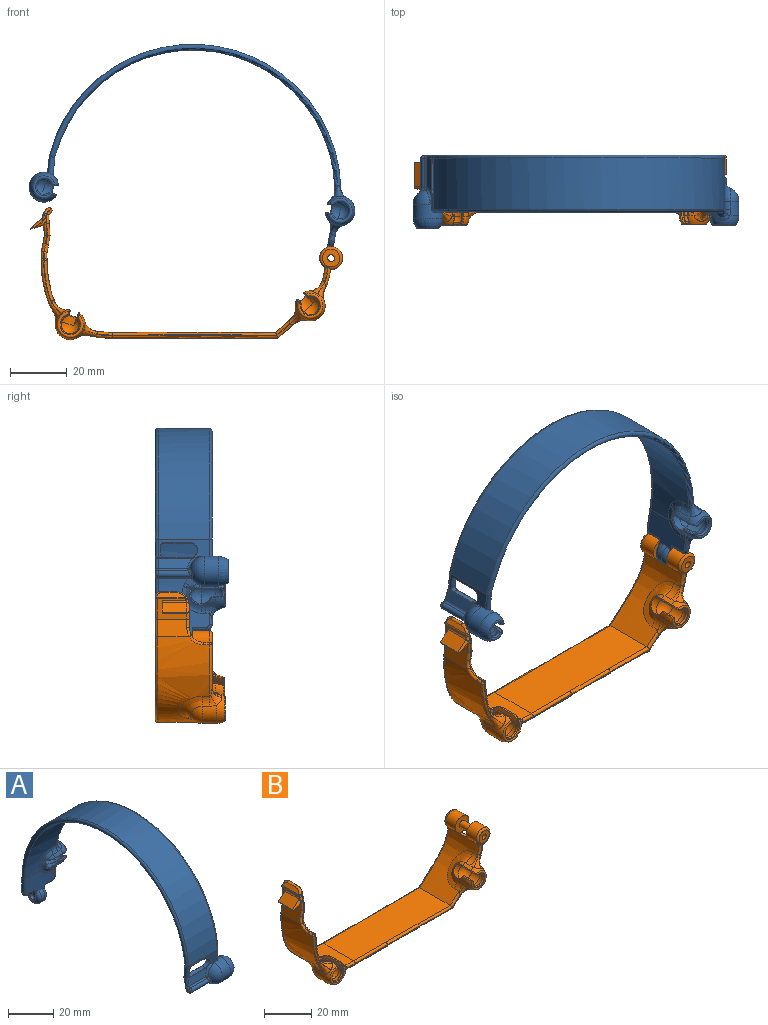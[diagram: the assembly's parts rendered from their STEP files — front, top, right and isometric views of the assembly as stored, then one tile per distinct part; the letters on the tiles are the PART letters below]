
ASSEMBLY  parts=2 mates=1
PART A: 128 faces, bbox 29x116.6x76.7 mm
  f0: cylinder r=5.25mm len=9.98mm, axis (-1,0,0), area 63.7mm2, adj f5,f82,f120,f122,f125,f127
  f1: cylinder r=5.25mm len=3.51mm, axis (-1,0,0), area 6.8mm2, adj f5,f100,f104,f119,f121
  f2: cylinder r=5.25mm len=5mm, axis (-1,0,0), area 9.6mm2, adj f5,f6,f94,f114,f116
  f3: sphere r=3.75mm, area 47.8mm2, adj f4,f7,f87,f103
  f4: cone r=2.84mm half-angle=32.6deg, axis (1,0,0), area 13.6mm2, adj f3,f86,f87,f88,f103,f105
  f5: revolved ~10.5x10.14mm, area 78.1mm2, adj f0,f1,f2,f86,f92,f106,f118,f123
  f6: sphere r=5.25mm, area 3.1mm2, adj f2,f96,f112
  f7: cylinder r=3.75mm len=7.5mm, axis (1,0,0), area 93.5mm2, adj f3,f8,f85,f89,f101
  f8: sphere r=3.75mm, area 55.5mm2, adj f7,f85,f91,f93
  f9: plane 18x11.74mm, normal (0,1,0), area 122.7mm2, adj f11,f14,f15,f37,f38,f60,f62,f63
  f10: plane 20.27x16.01mm, normal (0,-1,0), area 141.9mm2, adj f12,f14,f15,f37,f38,f60,f61,f62
  f11: cylinder r=52.06mm len=104mm, axis (1,0,0), area 2771.6mm2, adj f9,f13,f24,f59,f122,f124
  f12: cylinder r=50.06mm len=100mm, axis (1,0,0), area 2684.3mm2, adj f10,f13,f28,f59,f108,f110,f112,f113
  f13: torus R=51.06mm, axis (-1,0,0), area 457.9mm2, adj f11,f12,f64,f65,f116,f118,f120
  f14: cylinder r=1mm len=3.94mm, axis (0,0,-1), area 8.3mm2, adj f9,f10,f67,f68,f121,f123,f125
  f15: cylinder r=4mm len=8mm, axis (1,0,0), area 46.1mm2, adj f9,f10,f79,f80
  f16: cylinder r=5.25mm len=10.5mm, axis (1,0,0), area 135.3mm2, adj f17,f24,f30,f43,f46,f47,f64,f70
  f17: revolved ~10.49x10.21mm, area 97.9mm2, adj f16,f39,f42,f48
  f18: cone r=3.42mm half-angle=35.3deg, axis (1,0,0), area 11mm2, adj f19,f39,f40,f50
  f19: sphere r=3.75mm, area 55.1mm2, adj f18,f20,f31,f33,f40,f50
  f20: cylinder r=3.75mm len=7.5mm, axis (-1,0,0), area 94.9mm2, adj f19,f21,f31,f32,f33
  f21: sphere r=3.75mm, area 57.4mm2, adj f20,f32,f33
  f22: cylinder r=1.3mm len=11.27mm, axis (1,0,0), area 37.9mm2, adj f23,f53,f54,f71
  f23: cylinder r=1.8mm len=11.38mm, axis (1,0,0), area 28.9mm2, adj f22,f27,f52,f71
  f24: plane 18.05x6.4mm, normal (0,-1,-0.08), area 47.3mm2, adj f11,f16,f34,f35,f51,f58,f64,f74
  f25: plane 18x6.32mm, normal (0,1,0.08), area 46.8mm2, adj f28,f34,f35,f36,f51,f58,f64,f70
  f26: plane 12.36x3.83mm, normal (0,-0.98,0.21), area 43.1mm2, adj f54,f55,f74,f75
  f27: plane 14.84x6.26mm, normal (0,0.98,-0.21), area 75.5mm2, adj f23,f30,f55,f70,f71
  f28: plane 18x0.04mm, normal (0,0.84,0.55), area 0.8mm2, adj f12,f25,f57,f65
  f29: plane 2.2x1.72mm, normal (-1,0,0), area 1.2mm2, adj f52,f53,f55,f56
  f30: sphere r=5.25mm, area 110.6mm2, adj f16,f27,f44,f45,f70,f71,f75
  f31: plane 4.91x2.41mm, normal (0,0.04,1), area 5.9mm2, adj f19,f20,f32,f47,f48,f49,f50
  f32: cylinder r=3.75mm len=7.19mm, axis (0,-1,0.04), area 28.6mm2, adj f20,f21,f31,f33,f45,f46,f47
  f33: plane 11.85x4.62mm, normal (0,-0.04,-1), area 14.9mm2, adj f19,f20,f21,f32,f40,f41,f42,f43
  f34: plane 3.64x2.26mm, normal (1,0,0), area 7mm2, adj f24,f25,f76,f77
  f35: plane 9.04x1.99mm, normal (0,0.08,-1), area 18.1mm2, adj f24,f25,f77,f78
  f36: plane 9.01x2mm, normal (0,-0.08,1), area 18.1mm2, adj f25,f51,f74,f76
  f37: plane 6.9x4mm, normal (-1,0,0), area 12.7mm2, adj f9,f10,f62,f80,f81
  f38: plane 6.9x4mm, normal (1,0,0), area 12.7mm2, adj f9,f10,f66,f79,f81
  f39: torus R=3.5mm, axis (-1,0,0), area 19.5mm2, adj f17,f18,f41,f49
  f40: bspline ~2.06x1.78mm, area 0.3mm2, adj f18,f19,f33,f41
  f41: bspline ~1.15x0.5mm, area 0.4mm2, adj f33,f39,f40,f42
  f42: bspline ~5.4x2.59mm, area 2.2mm2, adj f17,f33,f41,f43
  f43: cylinder r=0.3mm len=5mm, axis (1,0,0), area 2.9mm2, adj f16,f33,f42,f44
  f44: torus R=4.61mm, axis (0,-0.04,-1), area 2.5mm2, adj f30,f33,f43,f45
  f45: torus R=4.05mm, axis (0,-1,0.04), area 6mm2, adj f30,f32,f33,f44,f46
  f46: bspline ~4.49x2.95mm, area 3.1mm2, adj f16,f32,f45,f47
  f47: cylinder r=0.3mm len=1.57mm, axis (1,0,0), area 0.9mm2, adj f16,f31,f32,f46,f48
  f48: bspline ~5.4x2.59mm, area 2.2mm2, adj f17,f31,f47,f49
  f49: bspline ~1.21x0.48mm, area 0.4mm2, adj f31,f39,f48,f50
  f50: bspline ~2.06x1.79mm, area 0.3mm2, adj f18,f19,f31,f49
  f51: cylinder r=2.99mm len=3.14mm, axis (0,1,0.08), area 9.4mm2, adj f24,f25,f36,f74,f78
  f52: torus R=0.8mm, axis (-1,0,0), area 3.2mm2, adj f23,f29,f53,f55
  f53: torus R=0.3mm, axis (-1,0,0), area 4.1mm2, adj f22,f29,f52,f56
  f54: cylinder r=1mm len=10.28mm, axis (1,0,0), area 11.5mm2, adj f22,f26,f56,f73
  f55: cylinder r=1mm len=6.62mm, axis (0,-0.21,-0.98), area 16.2mm2, adj f26,f27,f29,f52,f56,f69,f72
  f56: torus R=2mm, axis (-1,0,0), area 2.4mm2, adj f29,f53,f54,f55
  f57: cylinder r=1mm len=1.04mm, axis (0,0.55,-0.84), area 0.1mm2, adj f28,f58,f59
  f58: cylinder r=1mm len=6.8mm, axis (0,0.08,-1), area 19.9mm2, adj f24,f25,f57,f59,f69,f72
  f59: torus R=51.06mm, axis (-1,0,0), area 493.5mm2, adj f11,f12,f57,f58,f60
  f60: cylinder r=1mm len=7.83mm, axis (0,0,1), area 24.6mm2, adj f9,f10,f59,f61,f63
  f61: bspline ~2.69x2.5mm, area 4.4mm2, adj f10,f60,f62,f63
  f62: cylinder r=1mm len=5mm, axis (-1,0,0), area 15.7mm2, adj f9,f10,f37,f61,f63
  f63: bspline ~2.45x2.45mm, area 3.7mm2, adj f9,f60,f61,f62
  f64: cylinder r=1mm len=6.86mm, axis (0,-0.08,1), area 19.2mm2, adj f13,f16,f24,f25,f65,f70
  f65: cylinder r=1mm len=1.04mm, axis (0,-0.55,0.84), area 0.1mm2, adj f13,f28,f64
  f66: cylinder r=1mm len=5mm, axis (1,0,0), area 15.7mm2, adj f9,f10,f38,f67,f68
  f67: bspline ~2.69x2.5mm, area 4.4mm2, adj f10,f14,f66,f68
  f68: bspline ~2.45x2.45mm, area 3.7mm2, adj f9,f14,f66,f67
  f69: sphere r=1mm, area 0.3mm2, adj f55,f58,f70
  f70: cylinder r=1mm len=18mm, axis (1,0,0), area 4.6mm2, adj f16,f25,f27,f30,f64,f69
  f71: bspline ~3.86x3.82mm, area 5.4mm2, adj f22,f23,f27,f30,f73
  f72: bspline ~1.04x1.03mm, area 0.2mm2, adj f55,f58,f74
  f73: sphere r=1mm, area 0.9mm2, adj f54,f71,f75
  f74: cylinder r=1mm len=13.23mm, axis (-1,0,0), area 2.4mm2, adj f24,f26,f36,f51,f72,f75,f76
  f75: torus R=6.01mm, axis (0,0.98,-0.21), area 7.9mm2, adj f16,f24,f26,f30,f73,f74
  f76: cylinder r=1mm len=2.08mm, axis (0,-1,-0.08), area 3.1mm2, adj f24,f25,f34,f36,f74
  f77: cylinder r=1mm len=2.07mm, axis (0,1,0.08), area 3.1mm2, adj f24,f25,f34,f35
  f78: cylinder r=3mm len=2.96mm, axis (0,-1,-0.08), area 8.4mm2, adj f24,f25,f35,f51
  f79: torus R=2mm, axis (1,0,0), area 54.4mm2, adj f9,f10,f15,f38
  f80: torus R=2mm, axis (-1,0,0), area 54.4mm2, adj f9,f10,f15,f37
  f81: cylinder r=1.25mm len=6mm, axis (1,0,0), area 47.1mm2, adj f37,f38
  f82: sphere r=5.25mm, area 50.1mm2, adj f0,f124,f126
  f83: plane 11.39x2.97mm, normal (0,0,-1), area 11.8mm2, adj f87,f88,f89,f90,f91,f92,f94,f95
  f84: plane 4.52x1.96mm, normal (0,0,1), area 4.6mm2, adj f99,f101,f103,f104,f105,f106,f107
  f85: cylinder r=3.75mm len=7.11mm, axis (0,1,0), area 29.1mm2, adj f7,f8,f95,f98,f99,f100
  f86: torus R=3.81mm, axis (1,0,0), area 24.2mm2, adj f4,f5,f90,f107
  f87: torus R=3.63mm, axis (0,0,-1), area 0.9mm2, adj f3,f4,f83,f88,f89
  f88: bspline ~2.48x1.92mm, area 0.3mm2, adj f4,f83,f87,f90
  f89: cylinder r=0.3mm len=5mm, axis (1,0,0), area 1.7mm2, adj f7,f83,f87,f91
  f90: bspline ~1.26x0.51mm, area 0.5mm2, adj f83,f86,f88,f92
  f91: torus R=3.63mm, axis (0,0,-1), area 1.3mm2, adj f8,f83,f89,f93
  f92: bspline ~5.45x2.16mm, area 2mm2, adj f5,f83,f90,f94
  f93: bspline ~1.64x0.52mm, area 0.2mm2, adj f8,f91,f95
  f94: cylinder r=0.3mm len=5mm, axis (-1,0,0), area 2.9mm2, adj f2,f83,f92,f96
  f95: cylinder r=0.3mm len=3.29mm, axis (0,1,0), area 0.8mm2, adj f83,f85,f93,f97
  f96: torus R=4.61mm, axis (0,0,-1), area 2.2mm2, adj f6,f83,f94,f97,f110
  f97: bspline ~0.95x0.83mm, area 0.3mm2, adj f95,f96,f98,f108,f109
  f98: torus R=4.05mm, axis (0,1,0), area 5.3mm2, adj f85,f97,f100,f109,f113,f115
  f99: cylinder r=0.3mm len=1.25mm, axis (0,1,0), area 0.4mm2, adj f84,f85,f101,f102
  f100: bspline ~4.49x3.03mm, area 3mm2, adj f1,f85,f98,f102,f117
  f101: cylinder r=0.3mm len=1.64mm, axis (1,0,0), area 0.5mm2, adj f7,f84,f99,f103
  f102: sphere r=0.3mm, area 0.1mm2, adj f99,f100,f104
  f103: torus R=3.63mm, axis (0,0,1), area 0.9mm2, adj f3,f4,f84,f101,f105
  f104: cylinder r=0.3mm len=1.37mm, axis (-1,0,0), area 0.8mm2, adj f1,f84,f102,f106
  f105: bspline ~2.48x1.92mm, area 0.3mm2, adj f4,f84,f103,f107
  f106: bspline ~5.45x2.16mm, area 2mm2, adj f5,f84,f104,f107
  f107: bspline ~1.23x0.51mm, area 0.5mm2, adj f84,f86,f105,f106
  f108: bspline ~2.88x1.23mm, area 0.5mm2, adj f12,f97,f109,f110,f111
  f109: bspline ~0.46x0.45mm, area 0.1mm2, adj f97,f98,f108,f111
  f110: bspline ~3.27x2.63mm, area 2.3mm2, adj f12,f96,f108,f112
  f111: bspline ~2.55x1.03mm, area 0.8mm2, adj f108,f109,f113
  f112: bspline ~7.68x5.32mm, area 18.6mm2, adj f6,f12,f110,f114
  f113: bspline ~7.49x3.41mm, area 13.3mm2, adj f12,f98,f111,f115
  f114: cylinder r=4mm len=3.45mm, axis (1,0,0), area 10.2mm2, adj f2,f12,f112,f116
  f115: torus R=6.97mm, axis (0,-1,0), area 18.3mm2, adj f10,f98,f113,f117
  f116: bspline ~4.09x3.8mm, area 5.1mm2, adj f2,f13,f114,f118
  f117: bspline ~3.12x2.19mm, area 4.7mm2, adj f10,f100,f115,f119
  f118: bspline ~5.33x5.11mm, area 16.9mm2, adj f5,f13,f116,f120
  f119: cylinder r=4mm len=3.04mm, axis (-1,0,0), area 4.4mm2, adj f1,f10,f117,f121
  f120: bspline ~3.9x3.35mm, area 5.6mm2, adj f0,f13,f118,f122
  f121: bspline ~3.65x3.63mm, area 4.9mm2, adj f1,f14,f119,f123
  f122: cylinder r=4mm len=2.97mm, axis (-1,0,0), area 11.6mm2, adj f0,f11,f120,f124
  f123: bspline ~5.37x4.9mm, area 17.1mm2, adj f5,f14,f121,f125
  f124: bspline ~12.73x10.22mm, area 54.8mm2, adj f11,f82,f122,f126
  f125: bspline ~3.99x3.95mm, area 5.8mm2, adj f0,f14,f123,f127
  f126: torus R=8.34mm, axis (0,-1,0), area 33.6mm2, adj f9,f82,f124,f127
  f127: cylinder r=4mm len=3.61mm, axis (-1,0,0), area 12.4mm2, adj f0,f9,f125,f126
PART B: 192 faces, bbox 111.3x26.9x47.9 mm
  f0: bspline ~3.23x3.2mm, area 0.8mm2, adj f22,f187,f191
  f1: cylinder r=5.25mm len=5mm, axis (0,-1,0), area 16.9mm2, adj f14,f18,f136,f186,f188
  f2: cylinder r=5.25mm len=1.5mm, axis (0,-1,0), area 0.6mm2, adj f18,f128,f131,f191
  f3: cylinder r=5.25mm len=5mm, axis (0,-1,0), area 8.8mm2, adj f104,f105,f109,f148,f170,f172
  f4: cylinder r=5.25mm len=5mm, axis (0,-1,0), area 9.5mm2, adj f104,f105,f143,f171,f173
  f5: cylinder r=4mm len=8mm, axis (0,-1,0), area 134.9mm2, adj f7,f8,f48,f155
  f6: plane 68.31x4.23mm, normal (0,-1,0), area 14mm2, adj f9,f11,f24,f26,f83,f88,f166,f184
  f7: extruded ~24.21x18.51mm, area 414.3mm2, adj f5,f11,f12,f34,f35,f50,f154,f159
  f8: extruded ~22.82x18.2mm, area 376.3mm2, adj f5,f9,f10,f35,f36,f49,f154,f155
  f9: bspline ~8.48x7.61mm, area 9.3mm2, adj f6,f8,f83,f168,f170
  f10: bspline ~9.06x2.75mm, area 7.3mm2, adj f8,f13,f82,f169,f171
  f11: bspline ~7.89x7.09mm, area 9.9mm2, adj f6,f7,f88,f162,f164
  f12: bspline ~9.59x3.31mm, area 9.6mm2, adj f7,f13,f82,f163,f165
  f13: plane 11.85x6.2mm, normal (0,-1,0), area 26.5mm2, adj f10,f12,f82,f157,f167
  f14: sphere r=5.25mm, area 10.5mm2, adj f1,f132,f134,f135,f190
  f15: cylinder r=5.25mm len=8.29mm, axis (0,-1,0), area 60.9mm2, adj f18,f95,f175,f176,f179,f181
  f16: sphere r=3.75mm, area 37.8mm2, adj f19,f99,f117,f122
  f17: cone r=3mm half-angle=42.1deg, axis (0,-1,0), area 7.5mm2, adj f115,f116,f117,f118
  f18: revolved ~10.49x10.49mm, area 63mm2, adj f1,f2,f15,f116,f126,f137,f178,f180
  f19: cylinder r=3.75mm len=7.5mm, axis (0,1,0), area 93.9mm2, adj f16,f96,f99,f124,f125
  f20: plane 15.17x3.07mm, normal (0,-1,0), area 3.1mm2, adj f23,f25,f91,f180
  f21: extruded ~30.08x25.01mm, area 673.2mm2, adj f25,f26,f33,f34,f54,f92,f94,f175
  f22: extruded ~27.88x23mm, area 583.4mm2, adj f0,f23,f24,f36,f37,f53,f79,f84
  f23: bspline ~16.59x3.95mm, area 20.3mm2, adj f20,f22,f89,f182,f191
  f24: bspline ~7.08x1.52mm, area 7.7mm2, adj f6,f22,f83,f185,f186
  f25: bspline ~20.35x6.19mm, area 24.6mm2, adj f20,f21,f93,f176,f178
  f26: bspline ~10.95x2.43mm, area 10.2mm2, adj f6,f21,f88,f181,f183
  f27: plane 7.42x0.74mm, normal (0,-1,0), area 1.5mm2, adj f45,f46,f74,f76,f85,f87
  f28: plane 8.6x4.05mm, normal (-0.65,0,0.76), area 45.7mm2, adj f29,f42,f71,f75,f78
  f29: plane 9.13x0.33mm, normal (-0.96,0,-0.29), area 2.8mm2, adj f28,f30,f42,f78,f81
  f30: plane 8.6x4.5mm, normal (0.29,0,-0.96), area 40.4mm2, adj f29,f32,f42,f81
  f31: plane 104.17x43.26mm, normal (0,1,0), area 54.8mm2, adj f47,f48,f49,f50,f51,f52,f53,f54
  f32: plane 10.2x7.12mm, normal (-1,0,-0.07), area 45.4mm2, adj f30,f33,f42,f60,f66,f70,f71,f85
  f33: plane 11.13x6.21mm, normal (-0.99,0,0.17), area 65.2mm2, adj f21,f32,f56,f87,f90,f92
  f34: cylinder r=4958.52mm len=58.24mm, axis (0,-1,0), area 1060mm2, adj f7,f21,f52,f88
  f35: cylinder r=4mm len=8mm, axis (0,-1,0), area 134.9mm2, adj f7,f8,f82,f156
  f36: cylinder r=4960.52mm len=57.49mm, axis (0,-1,0), area 1046.2mm2, adj f8,f22,f51,f83
  f37: plane 11.09x6.31mm, normal (0.99,0,-0.17), area 66.3mm2, adj f22,f38,f55,f76,f79
  f38: plane 10.25x7.07mm, normal (1,0,0.07), area 70.4mm2, adj f37,f39,f57,f69,f72,f74
  f39: plane 9.32x1.21mm, normal (0.77,0,-0.63), area 12.8mm2, adj f38,f61,f64,f67,f69
  f40: plane 5x0.15mm, normal (0.63,0,0.77), area 1mm2, adj f45,f47,f62,f67
  f41: plane 9.62x1.55mm, normal (-0.77,0,0.63), area 17mm2, adj f58,f59,f62,f65,f66
  f42: plane 4.59x4.5mm, normal (0,1,0), area 7.1mm2, adj f28,f29,f30,f32,f71
  f43: plane 2.1x0.2mm, normal (-0.07,0,1), area 0.4mm2, adj f46,f86,f91,f94
  f44: plane 1.87x1.07mm, normal (0,-1,0), area 0.6mm2, adj f45,f78,f81
  f45: cylinder r=5mm len=5.3mm, axis (-0.77,0,0.63), area 2.7mm2, adj f27,f40,f44,f65,f69,f70,f72,f73
  f46: cylinder r=5mm len=5.08mm, axis (1,0,0.07), area 1.6mm2, adj f27,f43,f79,f84,f90,f92
  f47: cylinder r=2mm len=2mm, axis (0.77,0,-0.63), area 0.6mm2, adj f31,f40,f58,f64
  f48: torus R=3.1mm, axis (0,1,0), area 31.1mm2, adj f5,f31,f49,f50
  f49: bspline ~26.51x19.23mm, area 42.7mm2, adj f8,f31,f48,f51
  f50: bspline ~26.74x19.92mm, area 44.3mm2, adj f7,f31,f48,f52
  f51: torus R=4959.62mm, axis (0,1,0), area 81.5mm2, adj f31,f36,f49,f53
  f52: torus R=4959.42mm, axis (0,1,0), area 82.1mm2, adj f31,f34,f50,f54
  f53: bspline ~29.18x24.25mm, area 60.1mm2, adj f22,f31,f51,f55
  f54: bspline ~30.56x25.39mm, area 63.2mm2, adj f21,f31,f52,f56
  f55: cylinder r=0.9mm len=6.53mm, axis (-0.17,0,-0.99), area 9mm2, adj f31,f37,f53,f57
  f56: cylinder r=0.9mm len=6.46mm, axis (0.17,0,0.99), area 8.9mm2, adj f31,f33,f54,f60
  f57: cylinder r=0.9mm len=7.35mm, axis (0.07,0,-1), area 10mm2, adj f31,f38,f55,f61
  f58: torus R=1.1mm, axis (-0.77,0,0.63), area 3.7mm2, adj f41,f47,f59,f62
  f59: cylinder r=0.9mm len=1.27mm, axis (0.63,0,0.77), area 1.3mm2, adj f31,f41,f58,f63
  f60: cylinder r=0.9mm len=7.29mm, axis (-0.07,0,1), area 10.2mm2, adj f31,f32,f56,f63
  f61: cylinder r=0.9mm len=1.22mm, axis (-0.63,0,-0.77), area 0.9mm2, adj f31,f39,f57,f64
  f62: cylinder r=0.9mm len=5mm, axis (0,-1,0), area 7.1mm2, adj f40,f41,f58,f65
  f63: sphere r=0.9mm, area 0.5mm2, adj f59,f60,f66
  f64: torus R=1.1mm, axis (-0.77,0,0.63), area 3.7mm2, adj f39,f47,f61,f67
  f65: torus R=4.1mm, axis (-0.77,0,0.63), area 6.8mm2, adj f41,f45,f62,f68
  f66: cylinder r=0.9mm len=9.62mm, axis (0,-1,0), area 6.6mm2, adj f32,f41,f63,f68
  f67: cylinder r=0.9mm len=5mm, axis (0,1,0), area 7.1mm2, adj f39,f40,f64,f69
  f68: sphere r=0.9mm, area 0.6mm2, adj f65,f66,f70
  f69: torus R=4.1mm, axis (-0.77,0,0.63), area 6.4mm2, adj f38,f39,f45,f67,f72
  f70: bspline ~2.44x1.83mm, area 1mm2, adj f32,f45,f68,f73
  f71: cylinder r=0.9mm len=8.6mm, axis (0,1,0), area 7.1mm2, adj f28,f32,f42,f73
  f72: bspline ~3.36x1.53mm, area 4mm2, adj f38,f45,f69,f74
  f73: bspline ~2.18x1.64mm, area 2.1mm2, adj f45,f70,f71,f75
  f74: cylinder r=0.9mm len=4.36mm, axis (-0.07,0,1), area 6mm2, adj f27,f38,f72,f76
  f75: bspline ~1.4x1.4mm, area 0.3mm2, adj f28,f45,f73,f78
  f76: cylinder r=0.9mm len=3.31mm, axis (0.17,0,0.99), area 4.5mm2, adj f27,f37,f74,f79
  f77: bspline ~2.14x1.51mm, area 0mm2, adj f45,f80,f81
  f78: cylinder r=0.9mm len=4.54mm, axis (-0.76,0,-0.65), area 5.8mm2, adj f28,f29,f44,f75,f81
  f79: bspline ~3.37x1.68mm, area 4.5mm2, adj f22,f37,f46,f76,f84
  f80: bspline ~2.25x1.01mm, area 0.1mm2, adj f45,f77,f81,f85
  f81: cylinder r=0.9mm len=5.54mm, axis (0.96,0,0.29), area 5.7mm2, adj f29,f30,f44,f77,f78,f80,f85
  f82: torus R=3.1mm, axis (0,1,0), area 31.1mm2, adj f10,f12,f13,f35
  f83: torus R=4959.62mm, axis (0,1,0), area 81.5mm2, adj f6,f9,f24,f36
  f84: bspline ~5.5x3.47mm, area 7.8mm2, adj f22,f46,f79,f86
  f85: cylinder r=0.9mm len=4.41mm, axis (0.07,0,-1), area 5.5mm2, adj f27,f32,f80,f81,f87
  f86: cylinder r=0.9mm len=2.1mm, axis (0,-1,0), area 3.1mm2, adj f22,f43,f84,f89
  f87: cylinder r=0.9mm len=3.23mm, axis (-0.17,0,-0.99), area 4.3mm2, adj f27,f33,f85,f90
  f88: torus R=4959.42mm, axis (0,1,0), area 82.1mm2, adj f6,f11,f26,f34
  f89: sphere r=0.9mm, area 1.3mm2, adj f23,f86,f91
  f90: bspline ~4.9x2.07mm, area 4.2mm2, adj f33,f46,f87,f92
  f91: cylinder r=0.9mm len=0.91mm, axis (-1,0,-0.07), area 0.3mm2, adj f20,f43,f89,f93
  f92: bspline ~6.88x4.28mm, area 7.4mm2, adj f21,f33,f46,f90,f94
  f93: sphere r=0.9mm, area 0.8mm2, adj f25,f91,f94
  f94: cylinder r=0.9mm len=2.1mm, axis (0,-1,0), area 2.9mm2, adj f21,f43,f92,f93
  f95: sphere r=5.25mm, area 346.4mm2, adj f15,f177
  f96: sphere r=3.75mm, area 56mm2, adj f19,f98,f99,f133
  f97: plane 4.16x1.55mm, normal (0.95,0,-0.31), area 4mm2, adj f118,f120,f122,f123,f124,f126,f128,f129
  f98: cylinder r=3.75mm len=7.11mm, axis (-0.31,0,-0.95), area 28.5mm2, adj f96,f125,f129,f131,f132,f133
  f99: plane 12.16x4.42mm, normal (-0.95,0,0.31), area 13.4mm2, adj f16,f19,f96,f115,f117,f133,f135,f136
  f100: sphere r=5.25mm, area 0mm2, adj f101,f159
  f101: cylinder r=5.25mm len=7.36mm, axis (0,-1,0), area 57mm2, adj f100,f104,f160,f161,f162,f163
  f102: sphere r=3.75mm, area 40.5mm2, adj f106,f110,f112,f151
  f103: cone r=2.84mm half-angle=49.9deg, axis (0,-1,0), area 5.2mm2, adj f111,f112,f113,f114
  f104: torus R=0mm, axis (0,-1,0), area 65.9mm2, adj f3,f4,f101,f113,f142,f147,f164,f165
  f105: sphere r=5.25mm, area 8.9mm2, adj f3,f4,f109,f144,f174
  f106: cylinder r=3.75mm len=7.5mm, axis (0,1,0), area 94.5mm2, adj f102,f107,f109,f110,f150
  f107: sphere r=3.75mm, area 57.4mm2, adj f106,f109,f110
  f108: plane 4.18x1.24mm, normal (0.71,0,0.71), area 4mm2, adj f114,f146,f147,f148,f149,f150,f151,f152
  f109: cylinder r=3.75mm len=7.46mm, axis (0.71,0,-0.71), area 37.1mm2, adj f3,f105,f106,f107,f110,f144,f148,f149
  f110: plane 11.41x3.43mm, normal (-0.71,0,-0.71), area 14mm2, adj f102,f106,f107,f109,f111,f112,f141,f142
  f111: bspline ~2x1.97mm, area 0.5mm2, adj f103,f110,f112,f140
  f112: torus R=3.66mm, axis (0,1,0), area 13.9mm2, adj f102,f103,f110,f111,f152,f153
  f113: torus R=3.89mm, axis (0,1,0), area 21.3mm2, adj f103,f104,f140,f141,f145,f146
  f114: bspline ~1.63x1.63mm, area 0.5mm2, adj f103,f108,f145,f153
  f115: bspline ~2.69x2.65mm, area 0.6mm2, adj f17,f99,f117,f139
  f116: torus R=4.04mm, axis (0,1,0), area 25.4mm2, adj f17,f18,f121,f123,f138,f139
  f117: torus R=3.76mm, axis (0,1,0), area 12.6mm2, adj f16,f17,f99,f115,f119,f120
  f118: bspline ~2.29x2.12mm, area 0.5mm2, adj f17,f97,f119,f121
  f119: bspline ~0.74x0.42mm, area 0.1mm2, adj f117,f118,f120
  f120: bspline ~0.3x0.25mm, area 0mm2, adj f97,f117,f119,f122
  f121: bspline ~0.8x0.65mm, area 0.2mm2, adj f116,f118,f123
  f122: torus R=3.63mm, axis (0.95,0,-0.31), area 0.7mm2, adj f16,f97,f120,f124
  f123: bspline ~0.63x0.49mm, area 0.2mm2, adj f97,f116,f121,f126
  f124: cylinder r=0.3mm len=1.37mm, axis (0,1,0), area 0.5mm2, adj f19,f97,f122,f127
  f125: bspline ~3.79x3.48mm, area 0.7mm2, adj f19,f98,f127
  f126: bspline ~5.04x1.62mm, area 1.7mm2, adj f18,f97,f123,f128
  f127: sphere r=0.3mm, area 0mm2, adj f124,f125,f129
  f128: cylinder r=0.3mm len=1.37mm, axis (0,-1,0), area 0.8mm2, adj f2,f97,f126,f130
  f129: cylinder r=0.3mm len=0.99mm, axis (-0.31,0,-0.95), area 0.3mm2, adj f97,f98,f127,f130
  f130: sphere r=0.3mm, area 0.1mm2, adj f128,f129,f131
  f131: bspline ~4.49x3.44mm, area 1.8mm2, adj f2,f98,f130,f132,f187,f191
  f132: torus R=4.05mm, axis (-0.31,0,-0.95), area 4.2mm2, adj f14,f98,f131,f134,f189
  f133: cylinder r=0.3mm len=3.19mm, axis (-0.31,0,-0.95), area 0.9mm2, adj f96,f98,f99,f134
  f134: bspline ~0.92x0.83mm, area 0.4mm2, adj f14,f132,f133,f135
  f135: torus R=4.61mm, axis (0.95,0,-0.31), area 2.2mm2, adj f14,f99,f134,f136
  f136: cylinder r=0.3mm len=5mm, axis (0,-1,0), area 2.9mm2, adj f1,f99,f135,f137
  f137: bspline ~5.04x1.62mm, area 1.7mm2, adj f18,f99,f136,f138
  f138: bspline ~0.69x0.55mm, area 0.2mm2, adj f99,f116,f137,f139
  f139: bspline ~1x0.43mm, area 0.2mm2, adj f115,f116,f138
  f140: bspline ~0.99x0.62mm, area 0.2mm2, adj f111,f113,f141
  f141: bspline ~0.59x0.58mm, area 0.1mm2, adj f110,f113,f140,f142
  f142: bspline ~4.84x1.53mm, area 1.8mm2, adj f104,f110,f141,f143
  f143: cylinder r=0.3mm len=5mm, axis (0,-1,0), area 2.9mm2, adj f4,f110,f142,f144
  f144: torus R=4.61mm, axis (0.71,0,0.71), area 2.2mm2, adj f105,f109,f110,f143
  f145: bspline ~0.99x0.62mm, area 0.2mm2, adj f113,f114,f146
  f146: bspline ~0.58x0.57mm, area 0.1mm2, adj f108,f113,f145,f147
  f147: bspline ~4.84x1.53mm, area 1.8mm2, adj f104,f108,f146,f148
  f148: cylinder r=0.3mm len=1.77mm, axis (0,-1,0), area 0.9mm2, adj f3,f108,f109,f147,f149
  f149: cylinder r=0.3mm len=1.19mm, axis (0.71,0,-0.71), area 0.4mm2, adj f108,f109,f148,f150
  f150: cylinder r=0.3mm len=1.64mm, axis (0,1,0), area 0.5mm2, adj f106,f108,f149,f151
  f151: torus R=3.63mm, axis (-0.71,0,-0.71), area 0.8mm2, adj f102,f108,f150,f152
  f152: bspline ~0.32x0.31mm, area 0mm2, adj f108,f112,f151,f153
  f153: bspline ~0.76x0.42mm, area 0.1mm2, adj f112,f114,f152
  f154: extruded ~6.5x1.96mm, area 15.3mm2, adj f7,f8,f155,f156
  f155: plane 8.25x8mm, normal (0,-1,0), area 42.3mm2, adj f5,f8,f154,f158
  f156: plane 8.25x8mm, normal (0,1,0), area 42.3mm2, adj f8,f35,f154,f158
  f157: cylinder r=1.25mm len=20mm, axis (0,1,0), area 157.1mm2, adj f13,f31
  f158: cylinder r=1.65mm len=6.5mm, axis (0,1,0), area 67.4mm2, adj f155,f156
  f159: bspline ~12.13x10.66mm, area 91.4mm2, adj f7,f100,f160,f161
  f160: cylinder r=5mm len=4.4mm, axis (0,-1,0), area 13.4mm2, adj f7,f101,f159,f162
  f161: cylinder r=5mm len=4.01mm, axis (0,-1,0), area 11.8mm2, adj f7,f101,f159,f163
  f162: bspline ~4.86x4.14mm, area 5.8mm2, adj f11,f101,f160,f164
  f163: bspline ~4.44x3.75mm, area 5.2mm2, adj f12,f101,f161,f165
  f164: bspline ~6.06x3.94mm, area 10.5mm2, adj f11,f104,f162,f166
  f165: bspline ~6.3x3.94mm, area 11.2mm2, adj f12,f104,f163,f167
  f166: torus R=9.54mm, axis (0,1,0), area 0.9mm2, adj f6,f104,f164,f168
  f167: torus R=9.54mm, axis (0,1,0), area 0.9mm2, adj f13,f104,f165,f169
  f168: bspline ~5.86x4.11mm, area 10.5mm2, adj f9,f104,f166,f170
  f169: bspline ~5.31x5.04mm, area 10.4mm2, adj f10,f104,f167,f171
  f170: bspline ~4.65x4mm, area 5.8mm2, adj f3,f9,f168,f172
  f171: bspline ~4.67x4.4mm, area 6.7mm2, adj f4,f10,f169,f173
  f172: cylinder r=5mm len=4.25mm, axis (0,-1,0), area 13.5mm2, adj f3,f8,f170,f174
  f173: cylinder r=5mm len=4.39mm, axis (0,-1,0), area 16.5mm2, adj f4,f8,f171,f174
  f174: bspline ~13.27x10.97mm, area 92.3mm2, adj f8,f105,f172,f173
  f175: cylinder r=5mm len=3.47mm, axis (0,-1,0), area 9.4mm2, adj f15,f21,f176,f177
  f176: bspline ~4.06x3.9mm, area 5.4mm2, adj f15,f25,f175,f178
  f177: bspline ~12.4x9.87mm, area 79.8mm2, adj f21,f95,f175,f179
  f178: bspline ~6.47x4.14mm, area 12.3mm2, adj f18,f25,f176,f180
  f179: cylinder r=5mm len=3.78mm, axis (0,-1,0), area 10.2mm2, adj f15,f21,f177,f181
  f180: torus R=9.68mm, axis (0,1,0), area 0.9mm2, adj f18,f20,f178,f182
  f181: bspline ~4.46x4.13mm, area 5.7mm2, adj f15,f26,f179,f183
  f182: bspline ~5.69x5.14mm, area 10.5mm2, adj f18,f23,f180,f191
  f183: bspline ~6.55x4.15mm, area 11.6mm2, adj f18,f26,f181,f184
  f184: torus R=9.68mm, axis (0,1,0), area 0.9mm2, adj f6,f18,f183,f185
  f185: bspline ~5.17x4.69mm, area 10.3mm2, adj f18,f24,f184,f186
  f186: bspline ~4.4x4.38mm, area 7.4mm2, adj f1,f24,f185,f188
  f187: bspline ~3.09x2.87mm, area 2.3mm2, adj f0,f131,f189
  f188: cylinder r=5mm len=4.03mm, axis (0,-1,0), area 15mm2, adj f1,f22,f186,f190
  f189: bspline ~8.64x6.22mm, area 35.1mm2, adj f22,f132,f187,f190
  f190: bspline ~9.88x9.42mm, area 56mm2, adj f14,f22,f188,f189
  f191: bspline ~5.85x5.77mm, area 16.3mm2, adj f0,f2,f22,f23,f131,f182
PLACE A rot(axis=(-0.09,0.09,-0.99),90.5deg) t=(22.76,71.67,49.13)mm
PLACE B rot(axis=(0.53,0.4,0.75),0deg) t=(8.38,199.47,31.55)mm fixed
MATE revolute A.f15 <-> B.f5  axis (0,1,0) through (109,47.67,56.78)mm
